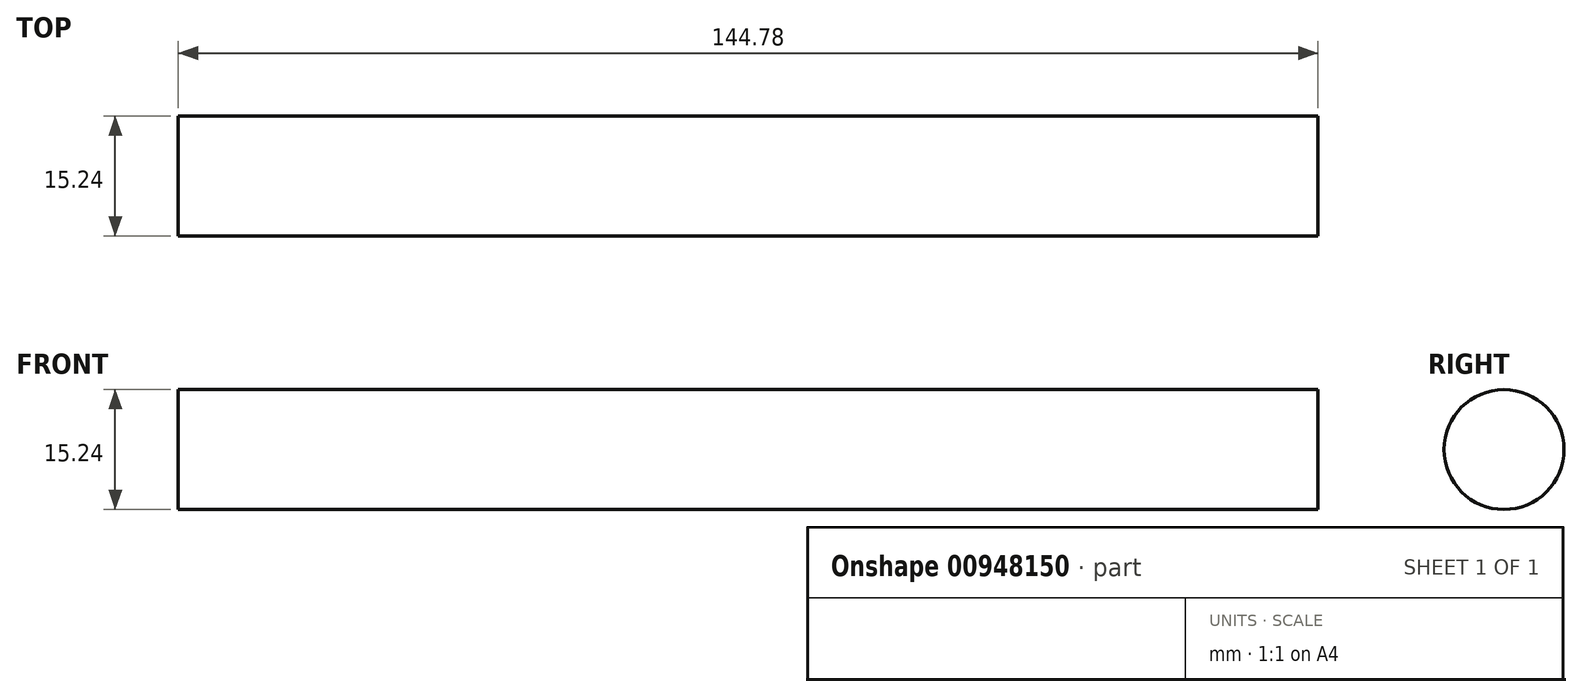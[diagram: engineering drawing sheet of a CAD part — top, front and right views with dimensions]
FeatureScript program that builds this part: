
annotation { "Feature Type Name" : "Feature", "Feature Type Description" : "" }
export const myFeature = defineFeature(function(context is Context, id is Id, definition is map)
    precondition{}
    {
        {
            var Q0;
            Q0=qCreatedBy(makeId("Right.planeOp"),FACE);
            var sketch = newSketch(context, id + "F0", { "sketchPlane" : qUnion([Q0])});
            skCircle(sketch, "E0", {"center": v(-33.4, 19) * mm, "radius": 7.62 * mm});
            skSolve(sketch);
        }
        {
            var Q0;
            Q0=makeQuery(id+"F0.imprint","IMPRINT",FACE,{"disambiguationData":[TD([[makeQuery(id+"F0.imprint","IMPRINT",EDGE,{"derivedFrom":sQuery(id+"F0.wireOp",EDGE,"E0")}),1.0]])]});
            extrude(context, id + "F1", {"entities" : qUnion([Q0]), "depth" : 144.78 * mm, "offsetDistance" : 25.4 * mm});
        }
    });
